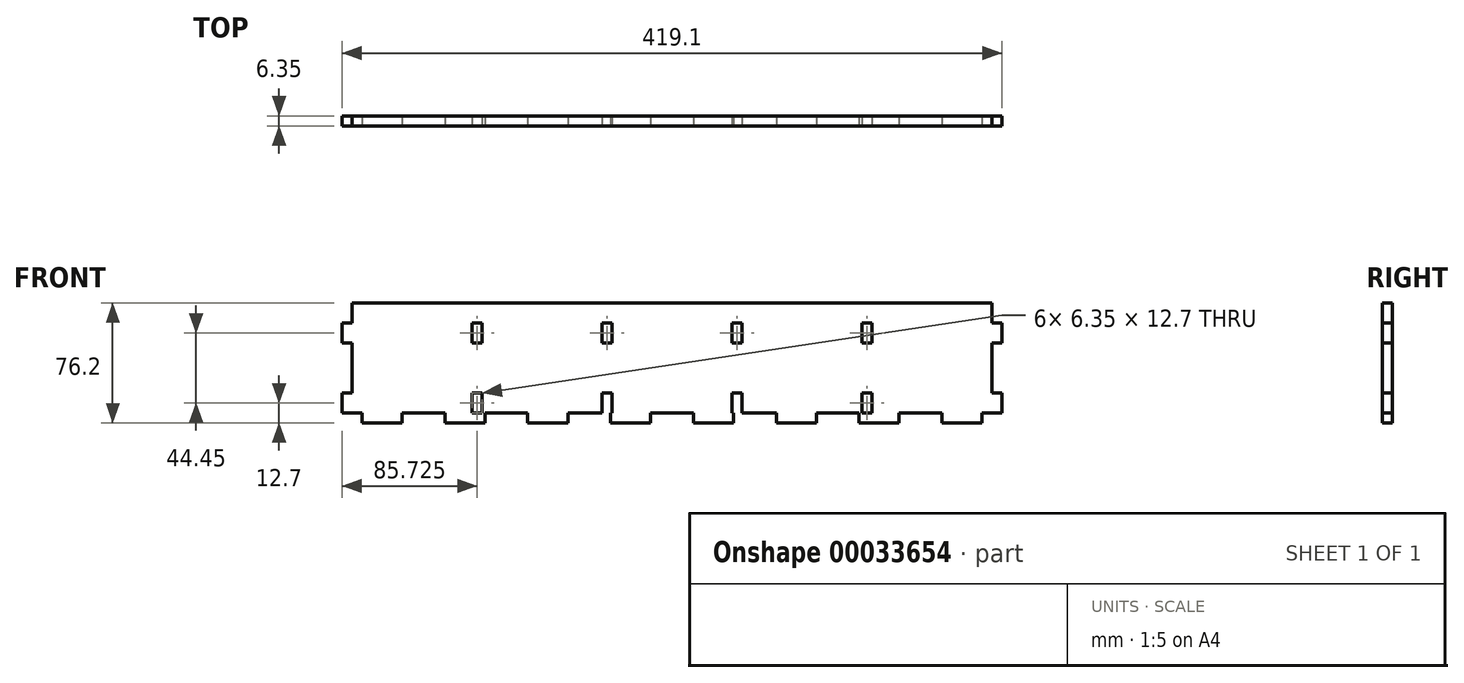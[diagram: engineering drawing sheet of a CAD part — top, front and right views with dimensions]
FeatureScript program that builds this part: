
annotation { "Feature Type Name" : "Feature", "Feature Type Description" : "" }
export const myFeature = defineFeature(function(context is Context, id is Id, definition is map)
    precondition{}
    {
        {
            var Q0;
            Q0=qCreatedBy(makeId("Front.planeOp"),FACE);
            var sketch = newSketch(context, id + "F0", { "sketchPlane" : qUnion([Q0])});
            skLineSegment(sketch, "E0.bottom", {"start": v(0, 0) * mm, "end": v(419.1, 0) * mm});
            skLineSegment(sketch, "E0.top", {"start": v(0, 76.2) * mm, "end": v(419.1, 76.2) * mm});
            skLineSegment(sketch, "E0.left", {"start": v(0, 0) * mm, "end": v(0, 76.2) * mm});
            skLineSegment(sketch, "E0.right", {"start": v(419.1, 0) * mm, "end": v(419.1, 76.2) * mm});
            skSolve(sketch);
        }
        {
            var Q0;
            Q0=makeQuery(id+"F0.imprint","IMPRINT",FACE,{"disambiguationData":[TD([[makeQuery(id+"F0.imprint","IMPRINT",EDGE,{"derivedFrom":sQuery(id+"F0.wireOp",EDGE,"E0.bottom")}),1.0]])]});
            extrude(context, id + "F1", {"entities" : qUnion([Q0]), "depth" : 6.35 * mm});
        }
        {
            var Q0;
            Q0=makeQuery(id+"F1.opExtrude","CAP_FACE",FACE,{"disambiguationData":[OSD([sQuery(id+"F0.wireOp",EDGE,"E0.bottom"),sQuery(id+"F0.wireOp",EDGE,"E0.top"),sQuery(id+"F0.wireOp",EDGE,"E0.left"),sQuery(id+"F0.wireOp",EDGE,"E0.right")])],"isStart":false});
            var sketch = newSketch(context, id + "F2", { "sketchPlane" : qUnion([Q0])});
            skLineSegment(sketch, "E1", {"start": v(209.55, 76.2) * mm, "end": v(209.55, 0) * mm, "construction": true});
            skLineSegment(sketch, "E2.bottom", {"start": v(0, 0) * mm, "end": v(6.35, 0) * mm});
            skLineSegment(sketch, "E2.top", {"start": v(0, 6.35) * mm, "end": v(6.35, 6.35) * mm});
            skLineSegment(sketch, "E2.left", {"start": v(0, 0) * mm, "end": v(0, 6.35) * mm});
            skLineSegment(sketch, "E2.right", {"start": v(6.35, 0) * mm, "end": v(6.35, 6.35) * mm});
            skLineSegment(sketch, "E3.bottom", {"start": v(0, 76.2) * mm, "end": v(6.35, 76.2) * mm});
            skLineSegment(sketch, "E3.top", {"start": v(0, 63.5) * mm, "end": v(6.35, 63.5) * mm});
            skLineSegment(sketch, "E3.left", {"start": v(0, 76.2) * mm, "end": v(0, 63.5) * mm});
            skLineSegment(sketch, "E3.right", {"start": v(6.35, 76.2) * mm, "end": v(6.35, 63.5) * mm});
            skLineSegment(sketch, "E4.bottom", {"start": v(0, 19.05) * mm, "end": v(6.35, 19.05) * mm});
            skLineSegment(sketch, "E4.top", {"start": v(0, 50.8) * mm, "end": v(6.35, 50.8) * mm});
            skLineSegment(sketch, "E4.left", {"start": v(0, 19.05) * mm, "end": v(0, 50.8) * mm});
            skLineSegment(sketch, "E4.right", {"start": v(6.35, 19.05) * mm, "end": v(6.35, 50.8) * mm});
            skLineSegment(sketch, "E5.MirrorCS", {"start": v(419.1, 6.35) * mm, "end": v(412.75, 6.35) * mm});
            skLineSegment(sketch, "E6.MirrorCS", {"start": v(419.1, 19.05) * mm, "end": v(412.75, 19.05) * mm});
            skLineSegment(sketch, "E7.MirrorCS", {"start": v(419.1, 50.8) * mm, "end": v(412.75, 50.8) * mm});
            skLineSegment(sketch, "E8.MirrorCS", {"start": v(419.1, 0) * mm, "end": v(412.75, 0) * mm});
            skLineSegment(sketch, "E9.MirrorCS", {"start": v(412.75, 76.2) * mm, "end": v(412.75, 63.5) * mm});
            skLineSegment(sketch, "E10.MirrorCS", {"start": v(412.75, 0) * mm, "end": v(412.75, 6.35) * mm});
            skLineSegment(sketch, "E11.MirrorCS", {"start": v(419.1, 0) * mm, "end": v(419.1, 6.35) * mm});
            skLineSegment(sketch, "E12.MirrorCS", {"start": v(419.1, 63.5) * mm, "end": v(412.75, 63.5) * mm});
            skLineSegment(sketch, "E13.MirrorCS", {"start": v(419.1, 76.2) * mm, "end": v(412.75, 76.2) * mm});
            skLineSegment(sketch, "E14.MirrorCS", {"start": v(419.1, 76.2) * mm, "end": v(419.1, 63.5) * mm});
            skLineSegment(sketch, "E15.MirrorCS", {"start": v(412.75, 19.05) * mm, "end": v(412.75, 50.8) * mm});
            skLineSegment(sketch, "E16.MirrorCS", {"start": v(419.1, 19.05) * mm, "end": v(419.1, 50.8) * mm});
            skSolve(sketch);
        }
        {
            var Q0;
            Q0=qSketchRegion(id+"F2",true);
            extrude(context, id + "F3", {"entities" : qUnion([Q0]), "operationType" : NewBodyOperationType.REMOVE, "endBound" : BoundingType.UP_TO_NEXT, "oppositeDirection" : true, "depth" : 25.4 * mm});
        }
        {
            var Q0;
            Q0=makeQuery(id+"F1.opExtrude","CAP_FACE",FACE,{"disambiguationData":[OSD([sQuery(id+"F0.wireOp",EDGE,"E0.bottom"),sQuery(id+"F0.wireOp",EDGE,"E0.top"),sQuery(id+"F0.wireOp",EDGE,"E0.left"),sQuery(id+"F0.wireOp",EDGE,"E0.right")])],"isStart":false});
            var sketch = newSketch(context, id + "F4", { "sketchPlane" : qUnion([Q0])});
            skLineSegment(sketch, "E17.bottom", {"start": v(38.1, 0) * mm, "end": v(65.31, 0) * mm});
            skLineSegment(sketch, "E17.top", {"start": v(38.1, 6.35) * mm, "end": v(65.31, 6.35) * mm});
            skLineSegment(sketch, "E17.left", {"start": v(38.1, 0) * mm, "end": v(38.1, 6.35) * mm});
            skLineSegment(sketch, "E17.right", {"start": v(65.31, 0) * mm, "end": v(65.31, 6.35) * mm});
            skLineSegment(sketch, "E18.1.0.0", {"start": v(117.93, 0) * mm, "end": v(117.93, 6.35) * mm});
            skLineSegment(sketch, "E18.1.0.1", {"start": v(90.71, 0) * mm, "end": v(90.71, 6.35) * mm});
            skLineSegment(sketch, "E18.1.0.2", {"start": v(90.71, 6.35) * mm, "end": v(117.93, 6.35) * mm});
            skLineSegment(sketch, "E18.1.0.3", {"start": v(90.71, 0) * mm, "end": v(117.93, 0) * mm});
            skLineSegment(sketch, "E18.2.0.0", {"start": v(170.54, 0) * mm, "end": v(170.54, 6.35) * mm});
            skLineSegment(sketch, "E18.2.0.1", {"start": v(143.33, 0) * mm, "end": v(143.33, 6.35) * mm});
            skLineSegment(sketch, "E18.2.0.2", {"start": v(143.33, 6.35) * mm, "end": v(170.54, 6.35) * mm});
            skLineSegment(sketch, "E18.2.0.3", {"start": v(143.33, 0) * mm, "end": v(170.54, 0) * mm});
            skLineSegment(sketch, "E18.3.0.0", {"start": v(223.16, 0) * mm, "end": v(223.16, 6.35) * mm});
            skLineSegment(sketch, "E18.3.0.1", {"start": v(195.94, 0) * mm, "end": v(195.94, 6.35) * mm});
            skLineSegment(sketch, "E18.3.0.2", {"start": v(195.94, 6.35) * mm, "end": v(223.16, 6.35) * mm});
            skLineSegment(sketch, "E18.3.0.3", {"start": v(195.94, 0) * mm, "end": v(223.16, 0) * mm});
            skLineSegment(sketch, "E18.4.0.0", {"start": v(275.77, 0) * mm, "end": v(275.77, 6.35) * mm});
            skLineSegment(sketch, "E18.4.0.1", {"start": v(248.56, 0) * mm, "end": v(248.56, 6.35) * mm});
            skLineSegment(sketch, "E18.4.0.2", {"start": v(248.56, 6.35) * mm, "end": v(275.77, 6.35) * mm});
            skLineSegment(sketch, "E18.4.0.3", {"start": v(248.56, 0) * mm, "end": v(275.77, 0) * mm});
            skLineSegment(sketch, "E18.direction1", {"start": v(65.31, 0) * mm, "end": v(117.93, 0) * mm, "construction": true});
            skLineSegment(sketch, "E19.0.5.0", {"start": v(328.39, 0) * mm, "end": v(328.39, 6.35) * mm});
            skLineSegment(sketch, "E19.3.5.0", {"start": v(301.17, 0) * mm, "end": v(301.17, 6.35) * mm});
            skLineSegment(sketch, "E19.6.5.0", {"start": v(301.17, 6.35) * mm, "end": v(328.39, 6.35) * mm});
            skLineSegment(sketch, "E19.9.5.0", {"start": v(301.17, 0) * mm, "end": v(328.39, 0) * mm});
            skLineSegment(sketch, "E19.0.6.0", {"start": v(381, 0) * mm, "end": v(381, 6.35) * mm});
            skLineSegment(sketch, "E19.3.6.0", {"start": v(353.79, 0) * mm, "end": v(353.79, 6.35) * mm});
            skLineSegment(sketch, "E19.6.6.0", {"start": v(353.79, 6.35) * mm, "end": v(381, 6.35) * mm});
            skLineSegment(sketch, "E19.9.6.0", {"start": v(353.79, 0) * mm, "end": v(381, 0) * mm});
            skLineSegment(sketch, "E20.bottom", {"start": v(6.35, 6.35) * mm, "end": v(12.7, 6.35) * mm});
            skLineSegment(sketch, "E20.top", {"start": v(6.35, 0) * mm, "end": v(12.7, 0) * mm});
            skLineSegment(sketch, "E20.left", {"start": v(6.35, 6.35) * mm, "end": v(6.35, 0) * mm});
            skLineSegment(sketch, "E20.right", {"start": v(12.7, 6.35) * mm, "end": v(12.7, 0) * mm});
            skLineSegment(sketch, "E21.bottom", {"start": v(412.75, 6.35) * mm, "end": v(406.4, 6.35) * mm});
            skLineSegment(sketch, "E21.top", {"start": v(412.75, 0) * mm, "end": v(406.4, 0) * mm});
            skLineSegment(sketch, "E21.left", {"start": v(412.75, 6.35) * mm, "end": v(412.75, 0) * mm});
            skLineSegment(sketch, "E21.right", {"start": v(406.4, 6.35) * mm, "end": v(406.4, 0) * mm});
            skSolve(sketch);
        }
        {
            var Q0;
            Q0=qSketchRegion(id+"F4",true);
            extrude(context, id + "F5", {"entities" : qUnion([Q0]), "operationType" : NewBodyOperationType.REMOVE, "endBound" : BoundingType.THROUGH_ALL, "oppositeDirection" : true, "depth" : 25.4 * mm});
        }
        {
            var Q0;
            Q0=makeQuery(id+"F1.opExtrude","CAP_FACE",FACE,{"disambiguationData":[OSD([sQuery(id+"F0.wireOp",EDGE,"E0.bottom"),sQuery(id+"F0.wireOp",EDGE,"E0.top"),sQuery(id+"F0.wireOp",EDGE,"E0.left"),sQuery(id+"F0.wireOp",EDGE,"E0.right")])],"isStart":false});
            var sketch = newSketch(context, id + "F6", { "sketchPlane" : qUnion([Q0])});
            skLineSegment(sketch, "E22.bottom", {"start": v(82.55, 6.35) * mm, "end": v(88.9, 6.35) * mm});
            skLineSegment(sketch, "E22.top", {"start": v(82.55, 19.05) * mm, "end": v(88.9, 19.05) * mm});
            skLineSegment(sketch, "E22.left", {"start": v(82.55, 6.35) * mm, "end": v(82.55, 19.05) * mm});
            skLineSegment(sketch, "E22.right", {"start": v(88.9, 6.35) * mm, "end": v(88.9, 19.05) * mm});
            skLineSegment(sketch, "E23", {"start": v(209.55, 76.2) * mm, "end": v(209.55, 6.35) * mm, "construction": true});
            skLineSegment(sketch, "E24.bottom", {"start": v(82.55, 50.8) * mm, "end": v(88.9, 50.8) * mm});
            skLineSegment(sketch, "E24.top", {"start": v(82.55, 63.5) * mm, "end": v(88.9, 63.5) * mm});
            skLineSegment(sketch, "E24.left", {"start": v(82.55, 50.8) * mm, "end": v(82.55, 63.5) * mm});
            skLineSegment(sketch, "E24.right", {"start": v(88.9, 50.8) * mm, "end": v(88.9, 63.5) * mm});
            skLineSegment(sketch, "E25.MirrorCS", {"start": v(330.2, 50.8) * mm, "end": v(330.2, 63.5) * mm});
            skLineSegment(sketch, "E26.MirrorCS", {"start": v(336.55, 50.8) * mm, "end": v(336.55, 63.5) * mm});
            skLineSegment(sketch, "E27.MirrorCS", {"start": v(336.55, 6.35) * mm, "end": v(330.2, 6.35) * mm});
            skLineSegment(sketch, "E28.MirrorCS", {"start": v(336.55, 19.05) * mm, "end": v(330.2, 19.05) * mm});
            skLineSegment(sketch, "E29.MirrorCS", {"start": v(336.55, 6.35) * mm, "end": v(336.55, 19.05) * mm});
            skLineSegment(sketch, "E30.MirrorCS", {"start": v(330.2, 6.35) * mm, "end": v(330.2, 19.05) * mm});
            skLineSegment(sketch, "E31.MirrorCS", {"start": v(336.55, 50.8) * mm, "end": v(330.2, 50.8) * mm});
            skLineSegment(sketch, "E32.MirrorCS", {"start": v(336.55, 63.5) * mm, "end": v(330.2, 63.5) * mm});
            skLineSegment(sketch, "E33.1.0.0", {"start": v(171.45, 50.8) * mm, "end": v(171.45, 63.5) * mm});
            skLineSegment(sketch, "E33.1.0.1", {"start": v(165.1, 50.8) * mm, "end": v(165.1, 63.5) * mm});
            skLineSegment(sketch, "E33.1.0.2", {"start": v(165.1, 63.5) * mm, "end": v(171.45, 63.5) * mm});
            skLineSegment(sketch, "E33.1.0.3", {"start": v(165.1, 50.8) * mm, "end": v(171.45, 50.8) * mm});
            skLineSegment(sketch, "E33.1.0.4", {"start": v(171.45, 6.35) * mm, "end": v(171.45, 19.05) * mm});
            skLineSegment(sketch, "E33.1.0.5", {"start": v(165.1, 6.35) * mm, "end": v(165.1, 19.05) * mm});
            skLineSegment(sketch, "E33.1.0.6", {"start": v(165.1, 19.05) * mm, "end": v(171.45, 19.05) * mm});
            skLineSegment(sketch, "E33.1.0.7", {"start": v(165.1, 6.35) * mm, "end": v(171.45, 6.35) * mm});
            skLineSegment(sketch, "E33.2.0.0", {"start": v(254, 50.8) * mm, "end": v(254, 63.5) * mm});
            skLineSegment(sketch, "E33.2.0.1", {"start": v(247.65, 50.8) * mm, "end": v(247.65, 63.5) * mm});
            skLineSegment(sketch, "E33.2.0.2", {"start": v(247.65, 63.5) * mm, "end": v(254, 63.5) * mm});
            skLineSegment(sketch, "E33.2.0.3", {"start": v(247.65, 50.8) * mm, "end": v(254, 50.8) * mm});
            skLineSegment(sketch, "E33.2.0.4", {"start": v(254, 6.35) * mm, "end": v(254, 19.05) * mm});
            skLineSegment(sketch, "E33.2.0.5", {"start": v(247.65, 6.35) * mm, "end": v(247.65, 19.05) * mm});
            skLineSegment(sketch, "E33.2.0.6", {"start": v(247.65, 19.05) * mm, "end": v(254, 19.05) * mm});
            skLineSegment(sketch, "E33.2.0.7", {"start": v(247.65, 6.35) * mm, "end": v(254, 6.35) * mm});
            skLineSegment(sketch, "E33.direction1", {"start": v(88.9, 50.8) * mm, "end": v(171.45, 50.8) * mm, "construction": true});
            skSolve(sketch);
        }
        {
            var Q0;
            Q0 = qSketchRegion(id + "F6", true);
            extrude(context, id + "F7", {"entities" : qUnion([Q0]), "operationType" : NewBodyOperationType.REMOVE, "endBound" : BoundingType.THROUGH_ALL, "oppositeDirection" : true, "depth" : 25.4 * mm});
        }
    });
